# Revit family: C_Reynaers_SL38 Ferro_Window Fixed
name_source: partatom
category: Windows
revit_build: Autodesk Revit 2015 (Build: 20150702_1515(x64)
units: mm (PartAtom-declared; Revit-internal decimal feet)

## types (1)
- Frame 38.5
    Analytic Construction = <None>
    BE = No
    BIMobject category = Windows
    Date of publishing = 2015-11-19
    Default Sill Height = 800 mm  [stored 2.62467 ft]
    Design country = Belgium
    Edition number = 1
    IFC Classification = Window
    Manufacturer = Reynaers
    Manufacturer country = Belgium
    Manufacturer name = Reynaers
    Material main = Aluminium
    Material secondary = Aluminium
    NBS Reference Code = 59-97
    NBS Reference Description = Windows
    NL = Yes
    Nominal height = 0
    Nominal width = 0
    Product Guid = e351ed82-0458-4031-8220-8276baccd360
    Product SKU = Reynaers_window_Slim_Line_38
    Product data url = https://bimobject.com
    Product family = Windows & Doors
    Product group = Windows Aluminium
    QR code = http://bimobject.com
    REY Built-In Depth = 86 mm
    REY Butt Strip Width = 10 mm  [stored 0.0328084 ft]
    REY Design = 0 mm  [stored 0 ft]
    REY Fixation Bottom = 38 mm  [stored 0.124672 ft]
    REY Frame Width = 39 mm
    REY Gap Width = 0 mm  [stored 0 ft]
    REY Joint Bottom = 5 mm  [stored 0.0164042 ft]
    REY Joint Width = 50 mm  [stored 0.164042 ft]
    REY Joint Width A = 50 mm  [stored 0.164042 ft]
    REY Joint Width B = 0 mm  [stored 0 ft]
    REY Offset Wall Ext Int = 0 mm  [stored 0 ft]
    REY Offset Wall Ext Int A = 0 mm  [stored 0 ft]
    REY Offset Wall Ext Int B = 50 mm  [stored 0.164042 ft]
    REY Panel Coverage = 10 mm  [stored 0.0328084 ft]
    REY Profile Rebate = 25 mm  [stored 0.082021 ft]
    REY Rebate = 10 mm  [stored 0.0328084 ft]
    REY Rebate A = 10 mm  [stored 0.0328084 ft]
    REY Rebate B = 0 mm  [stored 0 ft]
    REY Rebate TOP A = 10 mm  [stored 0.0328084 ft]
    REY Rebate TOP B = 0 mm  [stored 0 ft]
    REY Shutter = No
    REY Shutter Depth = 0 mm  [stored 0 ft]
    REY Shutter Height = 0 mm  [stored 0 ft]
    REY Shutter Position = 10 mm  [stored 0.0328084 ft]
    REY Shutter Roll Height = 200 mm  [stored 0.656168 ft]
    REY Shutter Roll Material = <By Category>
    REY Sill = No
    REY Sill H = 0 mm  [stored 0 ft]
    REY Sill Height = 35 mm  [stored 0.114829 ft]
    REY Vent & Gap = 0 mm  [stored 0 ft]
    REY Vent Width = 0 mm  [stored 0 ft]
    REY Website = www.reynaers.com
    UNSPSC Code = 301716
    URL = http://www.reynaers.com
    Uniclass 1.4 Code = JL10
    Uniclass 1.4 Description = Windows
    Uniclass 2.0 Code = PR-59-97
    Uniclass 2.0 Description = Windows
    Wall Closure = By host
    Wall Exterior Width = 90 mm  [stored 0.295276 ft]
    Weight Net (Kg) = 0

note: [stored X ft] marks values corroborated as IEEE doubles in the binary element streams (Revit-internal decimal feet)

## geometry (parser evidence)
native form markers: Blend x4, Sweep x3
no freeform markers — native parametric forms only
